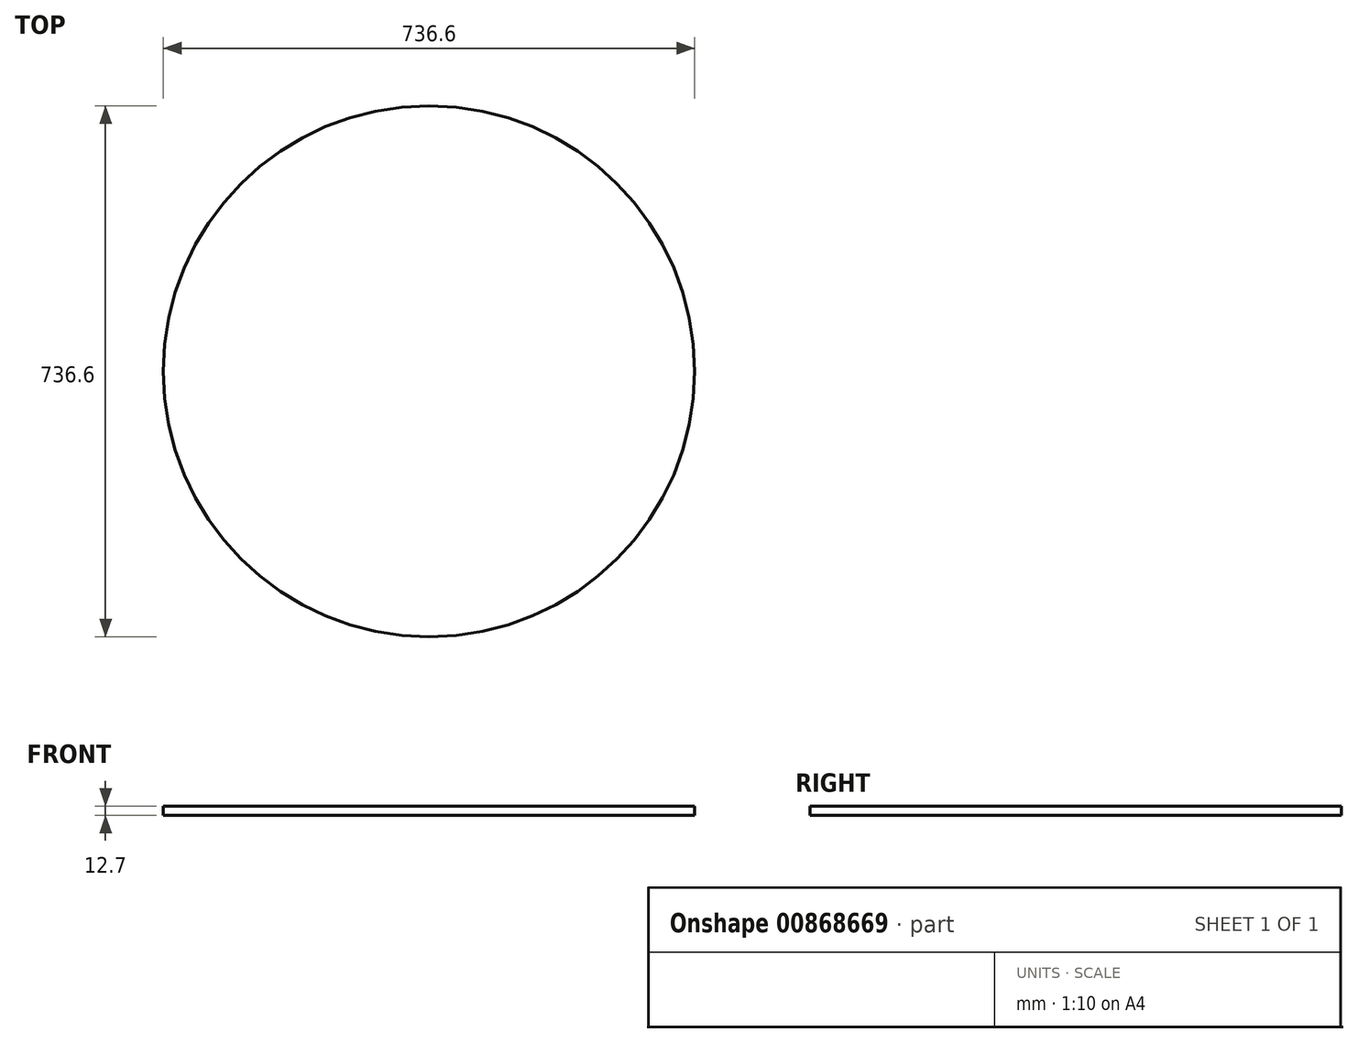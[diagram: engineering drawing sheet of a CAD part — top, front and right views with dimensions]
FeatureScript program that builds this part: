
annotation { "Feature Type Name" : "Feature", "Feature Type Description" : "" }
export const myFeature = defineFeature(function(context is Context, id is Id, definition is map)
    precondition{}
    {
        {
            var Q0;
            Q0=qCreatedBy(makeId("Top.planeOp"),FACE);
            var sketch = newSketch(context, id + "F0", { "sketchPlane" : qUnion([Q0])});
            skLineSegment(sketch, "E0.bottom", {"start": v(374.65, -370.84) * mm, "end": v(-374.65, -370.84) * mm, "construction": true});
            skLineSegment(sketch, "E0.top", {"start": v(374.65, 370.84) * mm, "end": v(-374.65, 370.84) * mm, "construction": true});
            skLineSegment(sketch, "E0.left", {"start": v(374.65, -370.84) * mm, "end": v(374.65, 370.84) * mm, "construction": true});
            skLineSegment(sketch, "E0.right", {"start": v(-374.65, -370.84) * mm, "end": v(-374.65, 370.84) * mm, "construction": true});
            skPoint(sketch, "E0.middle", {"position": v(0, 0) * mm});
            skCircle(sketch, "E1", {"center": v(0, 0) * mm, "radius": 368.3 * mm});
            skSolve(sketch);
        }
        {
            var Q0;
            Q0 = qSketchRegion(id + "F0", true);
            extrude(context, id + "F1", {"entities" : qUnion([Q0]), "depth" : 12.7 * mm, "offsetDistance" : 25.4 * mm});
        }
    });
